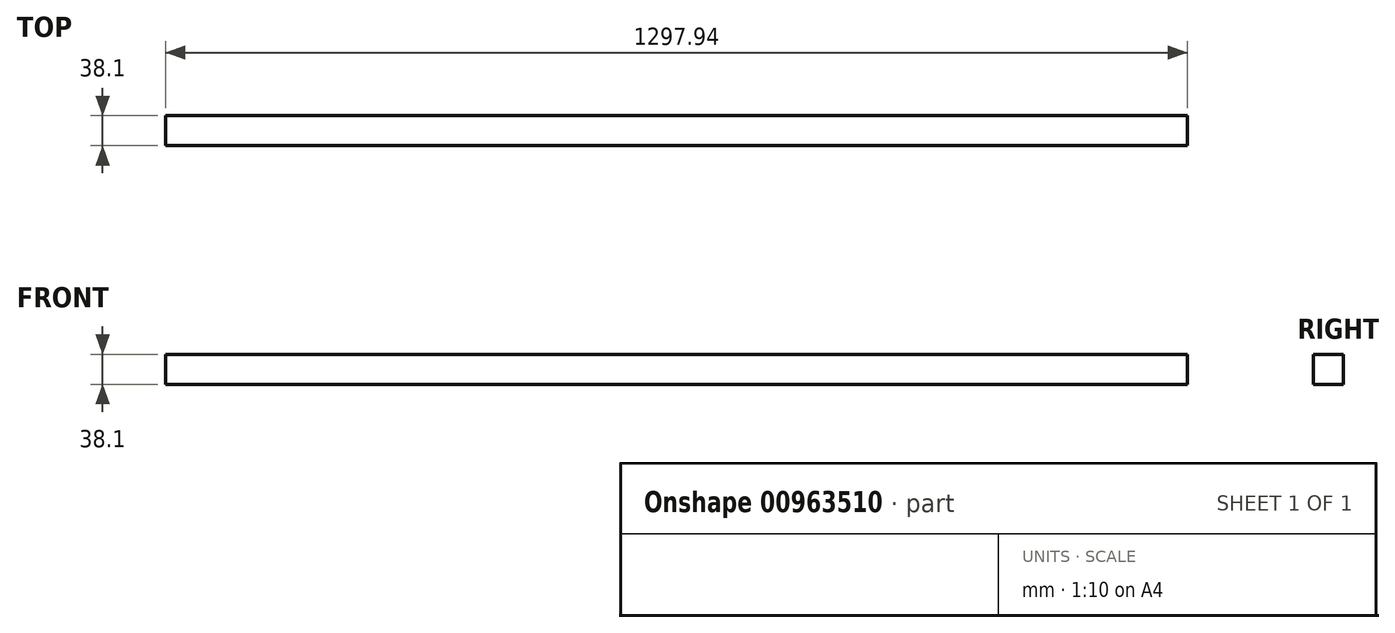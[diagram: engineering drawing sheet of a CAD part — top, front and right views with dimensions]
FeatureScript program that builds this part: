
annotation { "Feature Type Name" : "Feature", "Feature Type Description" : "" }
export const myFeature = defineFeature(function(context is Context, id is Id, definition is map)
    precondition{}
    {
        {
            var Q0;
            Q0=qCreatedBy(makeId("Front.planeOp"),FACE);
            var sketch = newSketch(context, id + "F0", { "sketchPlane" : qUnion([Q0])});
            skLineSegment(sketch, "E0.bottom", {"start": v(-648.97, 19.05) * mm, "end": v(648.97, 19.05) * mm});
            skLineSegment(sketch, "E0.top", {"start": v(-648.97, -19.05) * mm, "end": v(648.97, -19.05) * mm});
            skLineSegment(sketch, "E0.left", {"start": v(-648.97, 19.05) * mm, "end": v(-648.97, -19.05) * mm});
            skLineSegment(sketch, "E0.right", {"start": v(648.97, 19.05) * mm, "end": v(648.97, -19.05) * mm});
            skPoint(sketch, "E0.middle", {"position": v(0, 0) * mm});
            skSolve(sketch);
        }
        {
            var Q0;
            Q0=makeQuery(id+"F0.imprint","IMPRINT",FACE,{"disambiguationData":[TD([[makeQuery(id+"F0.imprint","IMPRINT",EDGE,{"derivedFrom":sQuery(id+"F0.wireOp",EDGE,"E0.bottom")}),-1.0]])]});
            extrude(context, id + "F1", {"entities" : qUnion([Q0]), "depth" : 38.1 * mm, "offsetDistance" : 25.4 * mm});
        }
    });
